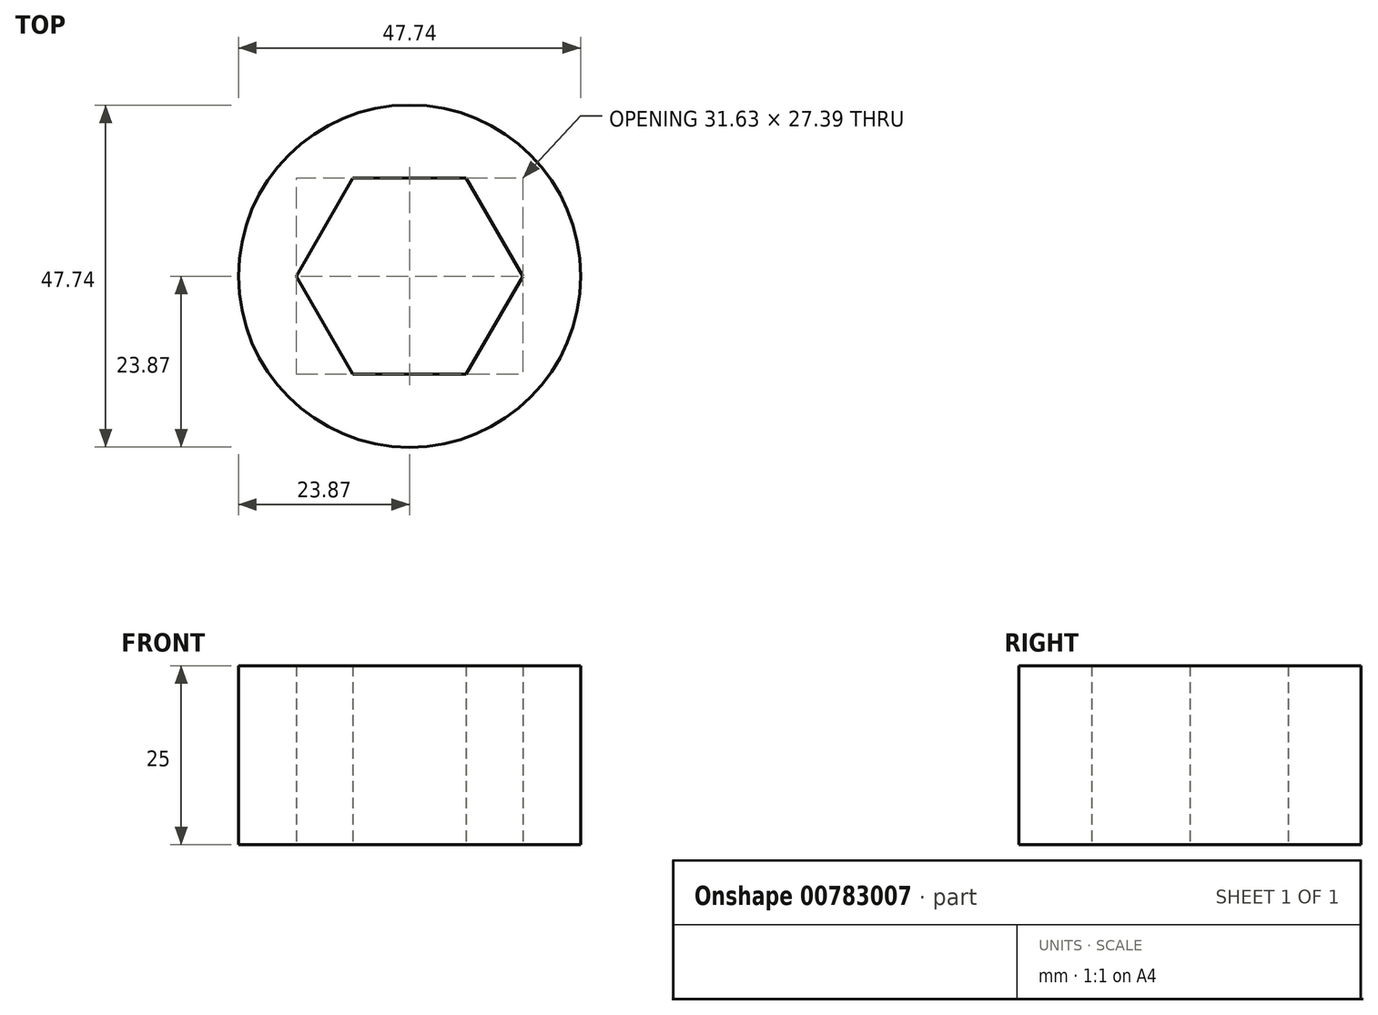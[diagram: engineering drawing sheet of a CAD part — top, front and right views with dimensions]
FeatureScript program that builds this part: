
annotation { "Feature Type Name" : "Feature", "Feature Type Description" : "" }
export const myFeature = defineFeature(function(context is Context, id is Id, definition is map)
    precondition{}
    {
        {
            var Q0;
            Q0=qCreatedBy(makeId("Top.planeOp"),FACE);
            var sketch = newSketch(context, id + "F0", { "sketchPlane" : qUnion([Q0])});
            skCircle(sketch, "E0", {"center": v(0, 0) * mm, "radius": 23.87 * mm});
            skCircle(sketch, "E1.cCircle", {"center": v(0, 0) * mm, "radius": 13.7 * mm, "construction": true});
            skLineSegment(sketch, "E1.0", {"start": v(15.82, 0) * mm, "end": v(7.9, -13.7) * mm});
            skLineSegment(sketch, "E1.1", {"start": v(7.9, -13.7) * mm, "end": v(-7.9, -13.7) * mm});
            skLineSegment(sketch, "E1.2", {"start": v(-7.9, -13.7) * mm, "end": v(-15.82, 0) * mm});
            skLineSegment(sketch, "E1.3", {"start": v(-15.82, 0) * mm, "end": v(-7.9, 13.7) * mm});
            skLineSegment(sketch, "E1.4", {"start": v(-7.9, 13.7) * mm, "end": v(7.9, 13.7) * mm});
            skLineSegment(sketch, "E1.5", {"start": v(7.9, 13.7) * mm, "end": v(15.82, 0) * mm});
            skPoint(sketch, "E1.0.midPoint", {"position": v(11.86, -6.85) * mm});
            skSolve(sketch);
        }
        {
            var Q0;
            Q0 = qSketchRegion(id + "F0", true);
            extrude(context, id + "F1", {"entities" : qUnion([Q0]), "depth" : 25 * mm, "offsetDistance" : 25 * mm});
        }
    });
